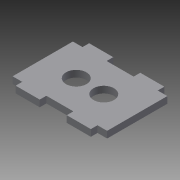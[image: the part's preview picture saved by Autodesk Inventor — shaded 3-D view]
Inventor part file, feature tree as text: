
AUTODESK INVENTOR PART (.ipt)
format: ipt  version: 2015 (Build 190159000, 159)  size: 106,496 bytes
history: native  units: mm
features: extrude x2, sketch x2
ambient origin geometry x8: Origin, YZ Plane, XZ Plane, XY Plane, X Axis, Y Axis, Z Axis, Center Point
bodies: Solid1 (feature_tree)
feature tree (4):
  extrude  "Extrusion1"  Depth=20.0mm
  extrude  "Extrusion2"  Depth=20.0mm
  sketch  "Sketch1"  dims[d2=5.5mm d3=20.0mm]
  sketch  "Sketch3"  dims[d4=5.5mm d5=20.0mm d6=90.0deg d16=5.5mm d17=0.0mm d18=8.0mm d20=8.0mm d22=17.0mm d23=17.0mm d24=10.0mm d25=0.0mm]
